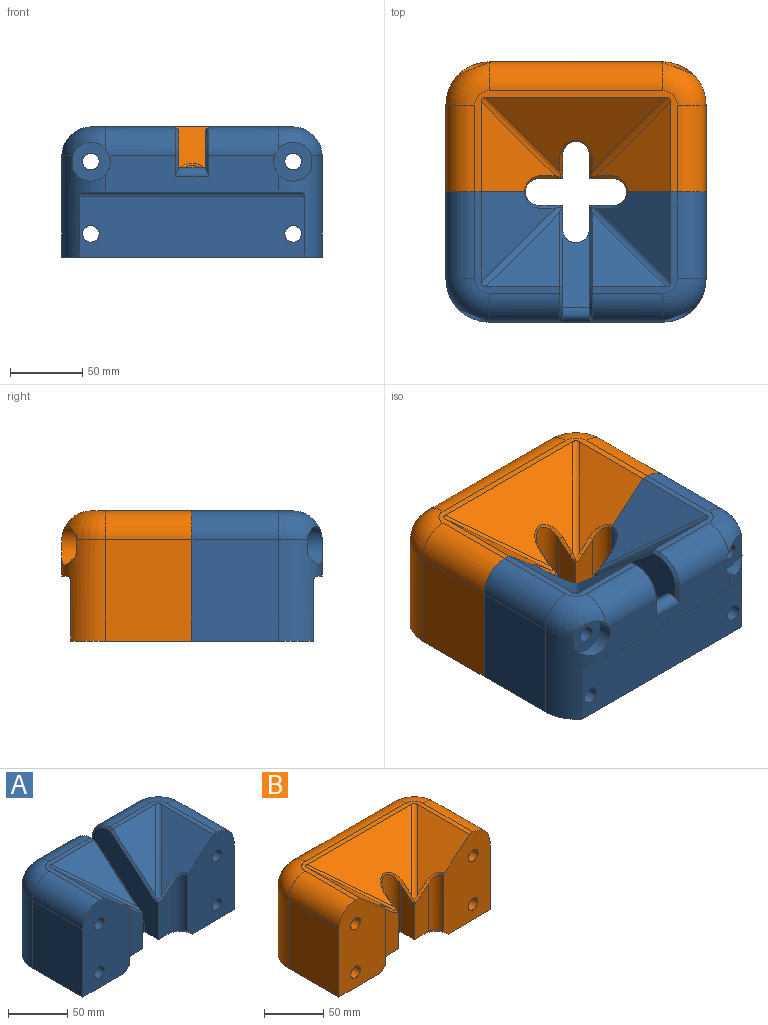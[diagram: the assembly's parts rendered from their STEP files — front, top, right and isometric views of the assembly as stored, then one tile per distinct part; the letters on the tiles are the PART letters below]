
ASSEMBLY  parts=2 mates=1
PART A: 65 faces, bbox 181.8x92.7x91.8 mm
  f0: cylinder r=5.75mm len=80mm, axis (0,-1,0), area 2890.3mm2, adj f16,f63
  f1: cylinder r=5.75mm len=80mm, axis (0,-1,0), area 2890.3mm2, adj f8,f64
  f2: plane 51.08x51.08mm, normal (0,-0.64,0.77), area 1703.2mm2, adj f14,f44,f49
  f3: plane 120x25mm, normal (0,1,0), area 2612.3mm2, adj f5,f10,f11,f19,f24,f25,f26,f46
  f4: plane 71.84x60.59mm, normal (0,0,1), area 534mm2, adj f5,f9,f16,f18,f22,f29,f43,f59
  f5: cylinder r=20mm len=48.75mm, axis (1,0,0), area 1524.1mm2, adj f3,f4,f22,f26,f60
  f6: cylinder r=9.25mm len=18.5mm, axis (0,0,-1), area 429.4mm2, adj f31,f32,f39,f45
  f7: plane 180x84mm, normal (0,0,-1), area 13247mm2, adj f8,f10,f11,f15,f16,f17,f23,f36
  f8: plane 90x55mm, normal (0,-1,0), area 4252.1mm2, adj f1,f7,f13,f14,f15,f20,f28,f34
  f9: plane 51.08x51.08mm, normal (0,-0.64,0.77), area 1703.2mm2, adj f4,f43,f58
  f10: cylinder r=30mm len=70mm, axis (0,0,1), area 2048mm2, adj f3,f7,f15,f21,f23,f24,f25,f27
  f11: cylinder r=30mm len=70mm, axis (0,0,-1), area 2048mm2, adj f3,f7,f17,f22,f23,f24,f26,f27
  f12: cylinder r=5.75mm len=84mm, axis (0,-1,0), area 3034.8mm2, adj f16,f23
  f13: cylinder r=5.75mm len=84mm, axis (0,-1,0), area 3034.8mm2, adj f8,f23
  f14: plane 71.84x60.59mm, normal (0,0,1), area 534mm2, adj f2,f8,f19,f20,f21,f28,f44,f48
  f15: plane 70x60mm, normal (-1,0,0), area 4200mm2, adj f7,f8,f10,f20
  f16: plane 90x55mm, normal (0,-1,0), area 4252.1mm2, adj f0,f4,f7,f12,f17,f18,f29,f30
  f17: plane 70x60mm, normal (1,0,0), area 4200mm2, adj f7,f11,f16,f18
  f18: cylinder r=20mm len=60mm, axis (0,-1,0), area 1885mm2, adj f4,f16,f17,f22
  f19: cylinder r=20mm len=48.75mm, axis (1,0,0), area 1524.1mm2, adj f3,f14,f21,f25,f47
  f20: cylinder r=20mm len=60mm, axis (0,1,0), area 1885mm2, adj f8,f14,f15,f21
  f21: torus R=10mm, axis (0,0,1), area 926.5mm2, adj f10,f14,f19,f20,f25,f64
  f22: torus R=10mm, axis (0,0,1), area 926.5mm2, adj f4,f5,f11,f18,f26,f63
  f23: plane 156x42mm, normal (0,1,0), area 6344.3mm2, adj f7,f10,f11,f12,f13,f27
  f24: plane 146.15x3mm, normal (0,0,-1), area 412.9mm2, adj f3,f10,f11,f27
  f25: cylinder r=13.5mm len=27mm, axis (0,1,0), area 456mm2, adj f3,f10,f19,f21,f64
  f26: cylinder r=13.5mm len=27mm, axis (0,1,0), area 456mm2, adj f3,f5,f11,f22,f63
  f27: cylinder r=3mm len=156mm, axis (1,0,0), area 711.9mm2, adj f10,f11,f23,f24
  f28: plane 62.35x51.1mm, normal (0.64,0,0.77), area 2176.6mm2, adj f8,f14,f44,f50,f52
  f29: plane 62.35x51.1mm, normal (-0.64,0,0.77), area 2176.6mm2, adj f4,f16,f43,f54,f55
  f30: cylinder r=9.25mm len=58.44mm, axis (0,0,-1), area 780.5mm2, adj f16,f33,f36,f54
  f31: plane 83.02x78.77mm, normal (1,0,0), area 2887.6mm2, adj f6,f35,f40,f45,f46,f47,f48,f49
  f32: plane 83.02x78.77mm, normal (-1,0,0), area 2887.6mm2, adj f6,f33,f38,f45,f57,f58,f59,f60
  f33: plane 49.02x16.52mm, normal (0,-1,0), area 698.6mm2, adj f30,f32,f37,f55,f56
  f34: cylinder r=9.25mm len=58.44mm, axis (0,0,-1), area 780.5mm2, adj f8,f35,f42,f50
  f35: plane 49.02x16.52mm, normal (0,-1,0), area 698.6mm2, adj f31,f34,f41,f52,f53
  f36: cone r=9.25mm half-angle=45deg, axis (0,0,-1), area 130.5mm2, adj f7,f16,f30,f37
  f37: plane 16.5x5mm, normal (0,-0.71,-0.71), area 99mm2, adj f7,f33,f36,f38
  f38: plane 16.5x5mm, normal (-0.71,0,-0.71), area 99mm2, adj f7,f32,f37,f39
  f39: cone r=9.25mm half-angle=45deg, axis (0,0,-1), area 261mm2, adj f6,f7,f38,f40
  f40: plane 16.5x5mm, normal (0.71,0,-0.71), area 99mm2, adj f7,f31,f39,f41
  f41: plane 16.5x5mm, normal (0,-0.71,-0.71), area 99mm2, adj f7,f35,f40,f42
  f42: cone r=9.25mm half-angle=45deg, axis (0,0,-1), area 130.5mm2, adj f7,f8,f34,f41
  f43: cylinder r=5mm len=56.82mm, axis (0.61,0.61,0.51), area 406.1mm2, adj f4,f9,f29,f56,f57
  f44: cylinder r=5mm len=56.82mm, axis (0.61,-0.61,-0.51), area 406.1mm2, adj f2,f14,f28,f51,f53
  f45: plane 54.39x45.64mm, normal (0,-0.64,0.77), area 1138.2mm2, adj f6,f31,f32,f62
  f46: plane 15.08x2.95mm, normal (0.71,0.71,0), area 31.2mm2, adj f3,f31,f47,f62
  f47: cone r=18mm half-angle=45deg, axis (-1,0,0), area 84.4mm2, adj f19,f31,f46,f48
  f48: plane 4.45x2mm, normal (0.71,0,0.71), area 11.6mm2, adj f14,f31,f47,f49
  f49: plane 51.81x44.4mm, normal (0.71,-0.45,0.54), area 187.6mm2, adj f2,f31,f48,f51
  f50: bspline ~12.13x11.34mm, area 41.7mm2, adj f8,f28,f34,f52
  f51: bspline ~7.19x5.06mm, area 15.1mm2, adj f31,f44,f49,f53
  f52: plane 11.29x9.92mm, normal (0.45,-0.71,0.54), area 36.9mm2, adj f28,f35,f50,f53
  f53: bspline ~7.19x5.06mm, area 15.1mm2, adj f35,f44,f51,f52
  f54: bspline ~11.25x11.25mm, area 41.7mm2, adj f16,f29,f30,f55
  f55: plane 11.29x9.92mm, normal (-0.45,-0.71,0.54), area 36.9mm2, adj f29,f33,f54,f56
  f56: bspline ~7.19x5.06mm, area 15.1mm2, adj f33,f43,f55,f57
  f57: bspline ~7.19x5.06mm, area 15.1mm2, adj f32,f43,f56,f58
  f58: plane 51.81x44.4mm, normal (-0.71,-0.45,0.54), area 187.6mm2, adj f9,f32,f57,f59
  f59: plane 4.45x2mm, normal (-0.71,0,0.71), area 11.6mm2, adj f4,f32,f58,f60
  f60: cone r=20mm half-angle=45deg, axis (1,0,0), area 84.4mm2, adj f5,f32,f59,f61
  f61: plane 15.08x2.95mm, normal (-0.71,0.71,0), area 31.2mm2, adj f3,f32,f60,f62
  f62: cylinder r=6mm len=22.5mm, axis (1,0,0), area 261.9mm2, adj f3,f31,f32,f45,f46,f61
  f63: plane 27.03x25.89mm, normal (0,1,0), area 460.3mm2, adj f0,f11,f22,f26
  f64: plane 27.03x25.89mm, normal (0,1,0), area 460.3mm2, adj f1,f10,f21,f25
PART B: 55 faces, bbox 181.8x92.7x91.8 mm
  f0: cylinder r=5.75mm len=80mm, axis (0,-1,0), area 2890.3mm2, adj f12,f54
  f1: cylinder r=5.75mm len=80mm, axis (0,-1,0), area 2890.3mm2, adj f3,f52
  f2: plane 180x84mm, normal (0,0,-1), area 13247mm2, adj f3,f6,f7,f11,f12,f13,f19,f31
  f3: plane 90x55mm, normal (0,-1,0), area 4252.1mm2, adj f1,f2,f9,f10,f11,f16,f22,f29
  f4: plane 124.68x51.1mm, normal (0,-0.64,0.77), area 4353.5mm2, adj f10,f38,f39,f45,f47,f49
  f5: plane 120x25mm, normal (0,1,0), area 2930mm2, adj f6,f7,f15,f20,f51,f53
  f6: cylinder r=30mm len=70mm, axis (0,0,1), area 2048mm2, adj f2,f5,f11,f17,f19,f20,f21,f51
  f7: cylinder r=30mm len=70mm, axis (0,0,-1), area 2048mm2, adj f2,f5,f13,f18,f19,f20,f21,f53
  f8: cylinder r=5.75mm len=84mm, axis (0,-1,0), area 3034.8mm2, adj f12,f19
  f9: cylinder r=5.75mm len=84mm, axis (0,-1,0), area 3034.8mm2, adj f3,f19
  f10: plane 141.84x71.84mm, normal (0,0,1), area 1168.2mm2, adj f3,f4,f12,f14,f15,f16,f17,f18
  f11: plane 70x60mm, normal (-1,0,0), area 4200mm2, adj f2,f3,f6,f16
  f12: plane 90x55mm, normal (0,-1,0), area 4252.1mm2, adj f0,f2,f8,f10,f13,f14,f23,f24
  f13: plane 70x60mm, normal (1,0,0), area 4200mm2, adj f2,f7,f12,f14
  f14: cylinder r=20mm len=60mm, axis (0,-1,0), area 1885mm2, adj f10,f12,f13,f18
  f15: cylinder r=20mm len=120mm, axis (1,0,0), area 3755.1mm2, adj f5,f10,f17,f18,f51,f53
  f16: cylinder r=20mm len=60mm, axis (0,1,0), area 1885mm2, adj f3,f10,f11,f17
  f17: torus R=10mm, axis (0,0,1), area 926.5mm2, adj f6,f10,f15,f16,f51,f52
  f18: torus R=10mm, axis (0,0,1), area 926.5mm2, adj f7,f10,f14,f15,f53,f54
  f19: plane 156x42mm, normal (0,1,0), area 6344.3mm2, adj f2,f6,f7,f8,f9,f21
  f20: plane 146.15x3mm, normal (0,0,-1), area 412.9mm2, adj f5,f6,f7,f21
  f21: cylinder r=3mm len=156mm, axis (1,0,0), area 711.9mm2, adj f6,f7,f19,f20
  f22: plane 62.35x51.1mm, normal (0.64,0,0.77), area 2176.6mm2, adj f3,f10,f39,f40,f41
  f23: plane 62.35x51.1mm, normal (-0.64,0,0.77), area 2176.6mm2, adj f10,f12,f38,f44,f46
  f24: cylinder r=9.25mm len=58.44mm, axis (0,0,-1), area 780.5mm2, adj f12,f28,f31,f44
  f25: plane 49.02x16.52mm, normal (1,0,0), area 698.7mm2, adj f26,f30,f35,f43,f45
  f26: cylinder r=9.25mm len=49mm, axis (0,0,-1), area 1423.8mm2, adj f25,f27,f34,f47
  f27: plane 49.02x16.52mm, normal (-1,0,0), area 698.7mm2, adj f26,f28,f33,f49,f50
  f28: plane 49.02x16.52mm, normal (0,-1,0), area 698.6mm2, adj f24,f27,f32,f46,f48
  f29: cylinder r=9.25mm len=58.44mm, axis (0,0,-1), area 780.5mm2, adj f3,f30,f37,f40
  f30: plane 49.02x16.52mm, normal (0,-1,0), area 698.6mm2, adj f25,f29,f36,f41,f42
  f31: cone r=9.25mm half-angle=45deg, axis (0,0,-1), area 130.5mm2, adj f2,f12,f24,f32
  f32: plane 16.5x5mm, normal (0,-0.71,-0.71), area 99mm2, adj f2,f28,f31,f33
  f33: plane 16.5x5mm, normal (-0.71,0,-0.71), area 99mm2, adj f2,f27,f32,f34
  f34: cone r=9.25mm half-angle=45deg, axis (0,0,-1), area 261mm2, adj f2,f26,f33,f35
  f35: plane 16.5x5mm, normal (0.71,0,-0.71), area 99mm2, adj f2,f25,f34,f36
  f36: plane 16.5x5mm, normal (0,-0.71,-0.71), area 99mm2, adj f2,f30,f35,f37
  f37: cone r=9.25mm half-angle=45deg, axis (0,0,-1), area 130.5mm2, adj f2,f3,f29,f36
  f38: cylinder r=5mm len=56.82mm, axis (0.61,0.61,0.51), area 406.1mm2, adj f4,f10,f23,f48,f50
  f39: cylinder r=5mm len=56.82mm, axis (0.61,-0.61,-0.51), area 406.1mm2, adj f4,f10,f22,f42,f43
  f40: bspline ~12.13x11.34mm, area 41.7mm2, adj f3,f22,f29,f41
  f41: plane 11.29x9.92mm, normal (0.45,-0.71,0.54), area 36.9mm2, adj f22,f30,f40,f42
  f42: bspline ~7.19x5.06mm, area 15.1mm2, adj f30,f39,f41,f43
  f43: bspline ~7.19x5.06mm, area 15.1mm2, adj f25,f39,f42,f45
  f44: bspline ~11.25x11.25mm, area 41.7mm2, adj f12,f23,f24,f46
  f45: plane 11.29x9.92mm, normal (0.71,-0.45,0.54), area 36.9mm2, adj f4,f25,f43,f47
  f46: plane 11.29x9.92mm, normal (-0.45,-0.71,0.54), area 36.9mm2, adj f23,f28,f44,f48
  f47: bspline ~22.5x11.25mm, area 83.3mm2, adj f4,f26,f45,f49
  f48: bspline ~7.19x5.06mm, area 15.1mm2, adj f28,f38,f46,f50
  f49: plane 11.29x9.92mm, normal (-0.71,-0.45,0.54), area 36.9mm2, adj f4,f27,f47,f50
  f50: bspline ~7.19x5.06mm, area 15.1mm2, adj f27,f38,f48,f49
  f51: cylinder r=13.5mm len=27mm, axis (0,1,0), area 456mm2, adj f5,f6,f15,f17,f52
  f52: plane 27.03x25.89mm, normal (0,1,0), area 460.3mm2, adj f1,f6,f17,f51
  f53: cylinder r=13.5mm len=27mm, axis (0,1,0), area 456mm2, adj f5,f7,f15,f18,f54
  f54: plane 27.03x25.89mm, normal (0,1,0), area 460.3mm2, adj f0,f7,f18,f53
PLACE A rot(axis=(0,0,1),180deg) t=(294.32,-49.43,-166.19)mm
PLACE B rot(axis=(0,0,-1),0deg) t=(114.32,130.57,-166.19)mm
MATE fastened B.f1 <-> A.f0  axis (0,-1,0) through (134.32,40.57,-100.19)mm
